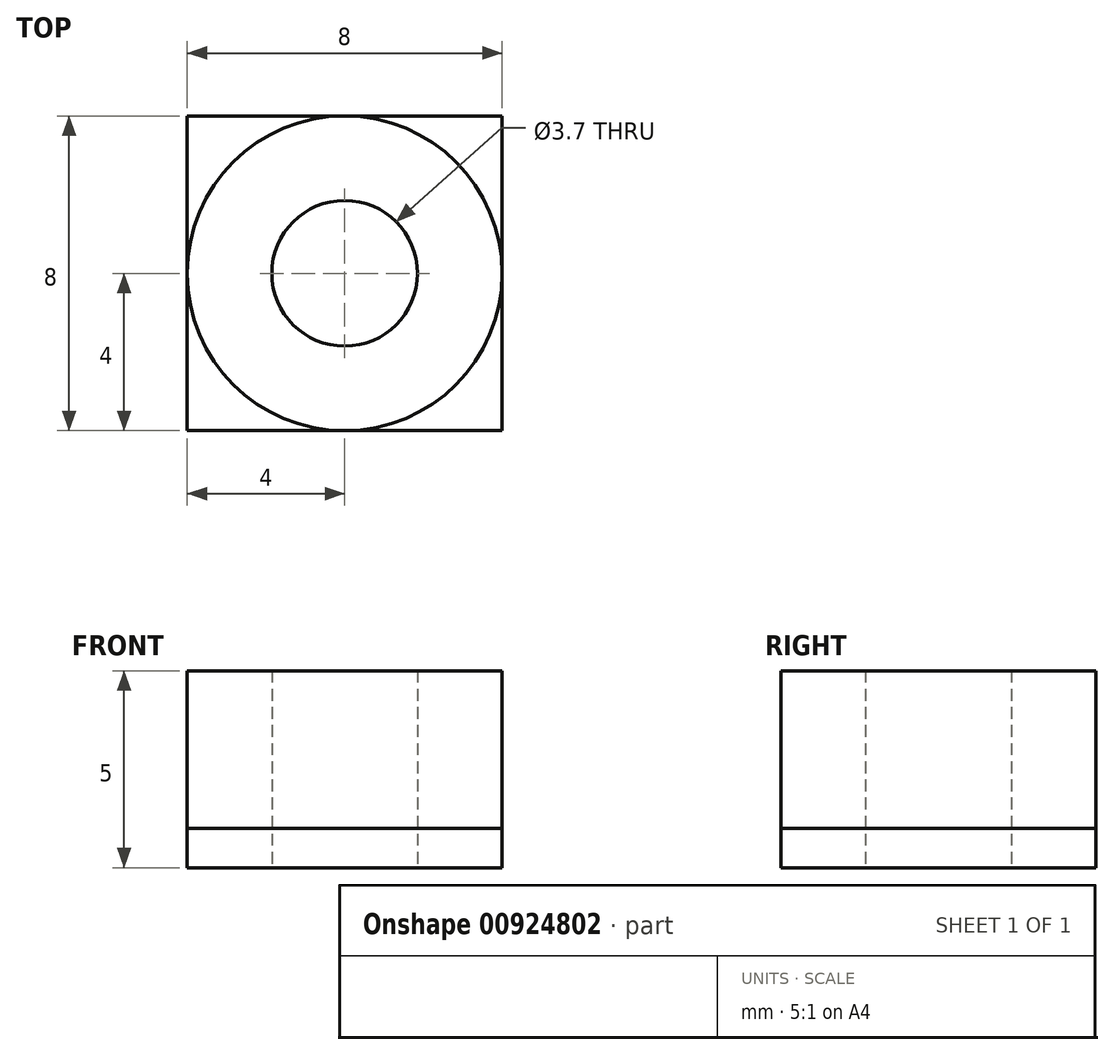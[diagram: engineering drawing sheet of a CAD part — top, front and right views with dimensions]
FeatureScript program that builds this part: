
annotation { "Feature Type Name" : "Feature", "Feature Type Description" : "" }
export const myFeature = defineFeature(function(context is Context, id is Id, definition is map)
    precondition{}
    {
        {
            var Q0;
            Q0=qCreatedBy(makeId("Top.planeOp"),FACE);
            var sketch = newSketch(context, id + "F0", { "sketchPlane" : qUnion([Q0])});
            skLineSegment(sketch, "E0.bottom", {"start": v(-4, 4) * mm, "end": v(4, 4) * mm});
            skLineSegment(sketch, "E0.top", {"start": v(-4, -4) * mm, "end": v(4, -4) * mm});
            skLineSegment(sketch, "E0.left", {"start": v(-4, 4) * mm, "end": v(-4, -4) * mm});
            skLineSegment(sketch, "E0.right", {"start": v(4, 4) * mm, "end": v(4, -4) * mm});
            skCircle(sketch, "E1", {"center": v(0, 0) * mm, "radius": 4 * mm});
            skCircle(sketch, "E2", {"center": v(0, 0) * mm, "radius": 1.85 * mm});
            skSolve(sketch);
        }
        {
            var Q0;
            Q0=makeQuery(id+"F0.imprint","IMPRINT",FACE,{"disambiguationData":[TD([[makeQuery(id+"F0.imprint","IMPRINT",EDGE,{"derivedFrom":sQuery(id+"F0.wireOp",EDGE,"E1")}),1.0]])]});
            var Q1;
            Q1=makeQuery(id+"F0.imprint","IMPRINT",FACE,{"disambiguationData":[TD([[makeQuery(id+"F0.imprint","IMPRINT",EDGE,{"derivedFrom":sQuery(id+"F0.wireOp",EDGE,"E0.bottom")}),-1.0]])]});
            var Q2;
            {var subQ0=sQuery(id+"F0.wireOp",EDGE,"E0.left");var subQ1=sQuery(id+"F0.wireOp",EDGE,"E0.top");var subQ2=makeQuery(id+"F0.imprint","INTERSECT",VERTEX,{"derivedFrom":[subQ1,subQ0]});Q2=makeQuery(id+"F0.imprint","IMPRINT",FACE,{"disambiguationData":[TD([[makeQuery(id+"F0.imprint","IMPRINT",EDGE,{"disambiguationData":[TD([[subQ2,-1.0]])],"derivedFrom":subQ1}),1.0]])]});}
            var Q3;
            {var subQ0=sQuery(id+"F0.wireOp",EDGE,"E0.right");var subQ1=sQuery(id+"F0.wireOp",EDGE,"E0.top");var subQ2=makeQuery(id+"F0.imprint","INTERSECT",VERTEX,{"derivedFrom":[subQ1,subQ0]});Q3=makeQuery(id+"F0.imprint","IMPRINT",FACE,{"disambiguationData":[TD([[makeQuery(id+"F0.imprint","IMPRINT",EDGE,{"disambiguationData":[TD([[subQ2,1.0]])],"derivedFrom":subQ1}),1.0]])]});}
            extrude(context, id + "F1", {"entities" : qUnion([Q0, Q1, Q2, Q3]), "depth" : 1 * mm, "offsetDistance" : 25 * mm});
        }
        {
            var Q0;
            Q0=makeQuery(id+"F0.imprint","IMPRINT",FACE,{"disambiguationData":[TD([[makeQuery(id+"F0.imprint","IMPRINT",EDGE,{"derivedFrom":sQuery(id+"F0.wireOp",EDGE,"E1")}),1.0]])]});
            extrude(context, id + "F2", {"entities" : qUnion([Q0]), "operationType" : NewBodyOperationType.ADD, "depth" : 5 * mm, "offsetDistance" : 25 * mm});
        }
    });
